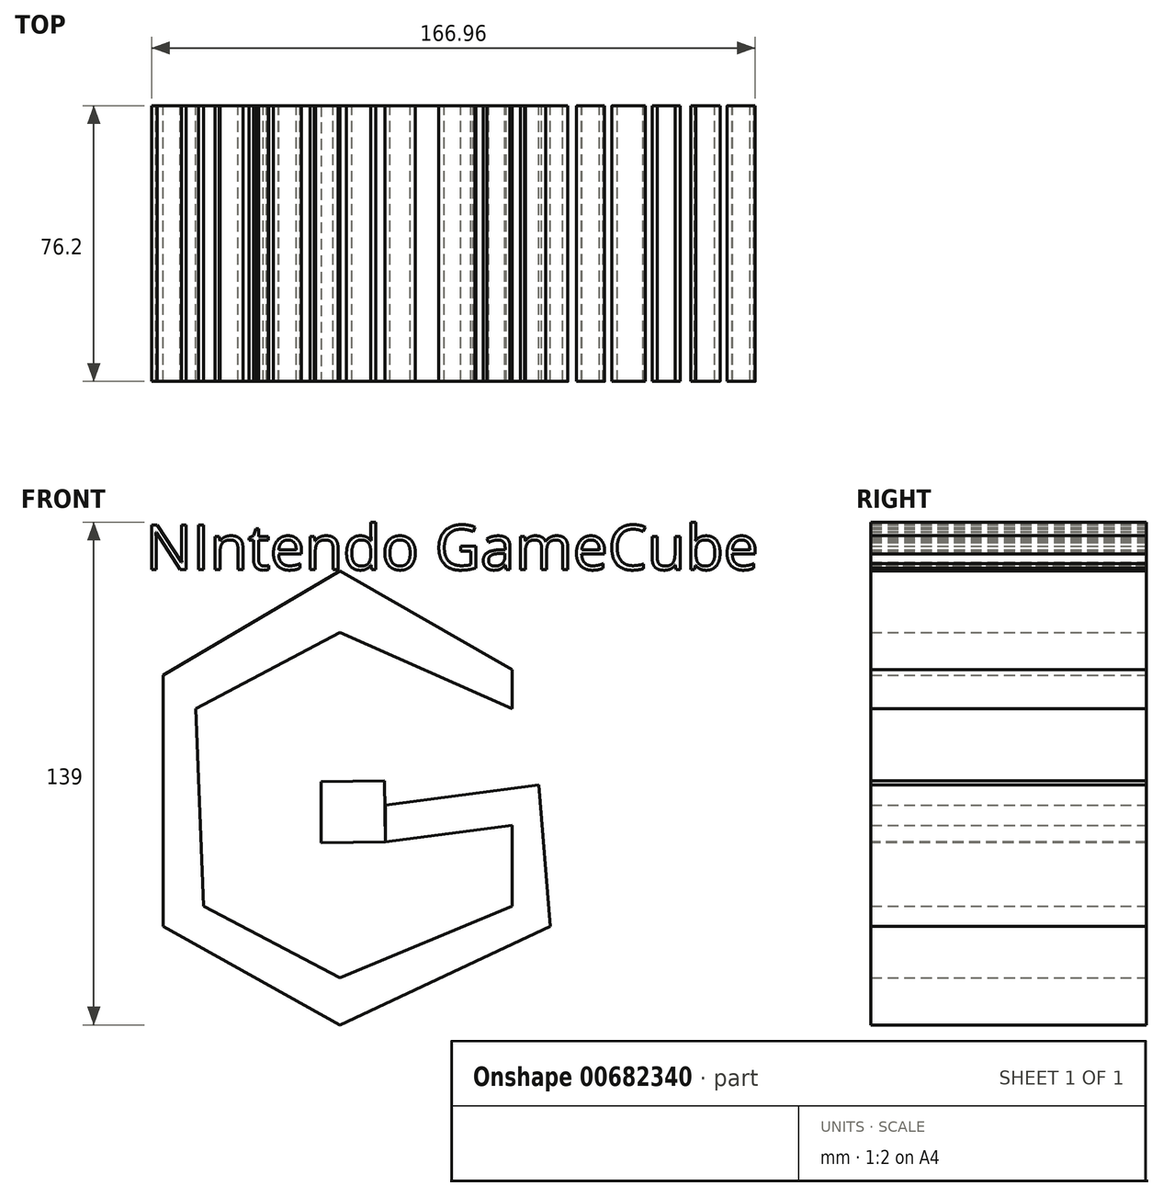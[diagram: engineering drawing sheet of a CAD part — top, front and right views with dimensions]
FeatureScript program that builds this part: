
annotation { "Feature Type Name" : "Feature", "Feature Type Description" : "" }
export const myFeature = defineFeature(function(context is Context, id is Id, definition is map)
    precondition{}
    {
        {
            var Q0;
            Q0=qCreatedBy(makeId("Front.planeOp"),FACE);
            var sketch = newSketch(context, id + "F0", { "sketchPlane" : qUnion([Q0])});
            skLineSegment(sketch, "E0", {"start": v(0, 54.12) * mm, "end": v(-48.84, 25.27) * mm});
            skLineSegment(sketch, "E1", {"start": v(0, 54.12) * mm, "end": v(47.6, 26.83) * mm});
            skLineSegment(sketch, "E2", {"start": v(-48.84, 25.27) * mm, "end": v(-48.84, -44.2) * mm});
            skLineSegment(sketch, "E3", {"start": v(-48.84, -44.2) * mm, "end": v(0, -71.48) * mm});
            skLineSegment(sketch, "E4", {"start": v(0, -71.48) * mm, "end": v(58.15, -44.2) * mm});
            skLineSegment(sketch, "E5", {"start": v(58.15, -44.2) * mm, "end": v(55.05, -5.12) * mm});
            skLineSegment(sketch, "E6", {"start": v(55.05, -5.12) * mm, "end": v(12.56, -10.7) * mm});
            skLineSegment(sketch, "E7", {"start": v(47.6, 26.83) * mm, "end": v(47.6, 15.97) * mm});
            skLineSegment(sketch, "E8", {"start": v(47.6, 15.97) * mm, "end": v(0, 37.06) * mm});
            skLineSegment(sketch, "E9", {"start": v(0, 37.06) * mm, "end": v(-39.85, 15.97) * mm});
            skLineSegment(sketch, "E10", {"start": v(-39.85, 15.97) * mm, "end": v(-37.68, -38.6) * mm});
            skLineSegment(sketch, "E11", {"start": v(-37.68, -38.6) * mm, "end": v(0, -58.46) * mm});
            skLineSegment(sketch, "E12", {"start": v(0, -58.46) * mm, "end": v(47.6, -38.6) * mm});
            skLineSegment(sketch, "E13", {"start": v(47.6, -38.6) * mm, "end": v(47.6, -16.28) * mm});
            skLineSegment(sketch, "E14", {"start": v(47.6, -16.28) * mm, "end": v(12.56, -20.89) * mm});
            skLineSegment(sketch, "E15", {"start": v(12.56, -10.7) * mm, "end": v(12.56, -20.89) * mm});
            skLineSegment(sketch, "E16", {"start": v(12.56, -20.89) * mm, "end": v(0, -20.89) * mm});
            skLineSegment(sketch, "E17", {"start": v(0, -20.89) * mm, "end": v(0, -5.12) * mm});
            skLineSegment(sketch, "E18", {"start": v(0, -5.12) * mm, "end": v(12.56, -10.7) * mm});
            skSolve(sketch);
        }
        {
            var Q0;
            Q0=makeQuery(id+"F0.imprint","IMPRINT",FACE,{"disambiguationData":[TD([[makeQuery(id+"F0.imprint","IMPRINT",EDGE,{"derivedFrom":sQuery(id+"F0.wireOp",EDGE,"E0")}),1.0]])]});
            extrude(context, id + "F1", {"entities" : qUnion([Q0]), "depth" : 76.2 * mm, "offsetDistance" : 25.4 * mm});
        }
        {
            var Q0;
            Q0=makeQuery(id+"F1.opExtrude","CAP_FACE",FACE,{"disambiguationData":[OSD([sQuery(id+"F0.wireOp",EDGE,"E0"),sQuery(id+"F0.wireOp",EDGE,"E1"),sQuery(id+"F0.wireOp",EDGE,"E2"),sQuery(id+"F0.wireOp",EDGE,"E3"),sQuery(id+"F0.wireOp",EDGE,"E4"),sQuery(id+"F0.wireOp",EDGE,"E5"),sQuery(id+"F0.wireOp",EDGE,"E6"),sQuery(id+"F0.wireOp",EDGE,"E7"),sQuery(id+"F0.wireOp",EDGE,"E8"),sQuery(id+"F0.wireOp",EDGE,"E9"),sQuery(id+"F0.wireOp",EDGE,"E10"),sQuery(id+"F0.wireOp",EDGE,"E11"),sQuery(id+"F0.wireOp",EDGE,"E12"),sQuery(id+"F0.wireOp",EDGE,"E13"),sQuery(id+"F0.wireOp",EDGE,"E14"),sQuery(id+"F0.wireOp",EDGE,"E15")])],"isStart":false});
            var sketch = newSketch(context, id + "F2", { "sketchPlane" : qUnion([Q0])});
            skLineSegment(sketch, "E19", {"start": v(-5.19, -4.21) * mm, "end": v(-5.19, -21.08) * mm});
            skLineSegment(sketch, "E20", {"start": v(-5.19, -21.08) * mm, "end": v(12.56, -20.89) * mm});
            skLineSegment(sketch, "E21", {"start": v(12.56, -20.89) * mm, "end": v(12.38, -3.96) * mm});
            skLineSegment(sketch, "E22", {"start": v(12.38, -3.96) * mm, "end": v(-5.19, -4.21) * mm});
            skSolve(sketch);
        }
        {
            var Q0;
            Q0=makeQuery(id+"F2.imprint","IMPRINT",FACE,{"disambiguationData":[TD([[makeQuery(id+"F2.imprint","IMPRINT",EDGE,{"derivedFrom":sQuery(id+"F2.wireOp",EDGE,"E19")}),1.0]])]});
            extrude(context, id + "F3", {"entities" : qUnion([Q0]), "oppositeDirection" : true, "depth" : 76.2 * mm, "offsetDistance" : 25.4 * mm});
        }
        {
            var Q0;
            Q0=qCreatedBy(makeId("Front.planeOp"),FACE);
            var sketch = newSketch(context, id + "F4", { "sketchPlane" : qUnion([Q0])});
            skText(sketch, "E23", { "text": "NIntendo GameCube", "fontName": "OpenSans-Regular.ttf"});
            const initialGuessF4  = {"E23": [-0.0538, 0.05443, 1, 0, 0.0124]};
            skSetInitialGuess(sketch, initialGuessF4);
            skSolve(sketch);
        }
        {
            var Q0;
            Q0 = qSketchRegion(id + "F4", true);
            extrude(context, id + "F5", {"entities" : qUnion([Q0]), "depth" : 76.2 * mm, "offsetDistance" : 25.4 * mm});
        }
    });
